# Revit family: Wenger Cabinet 04
name_source: partatom
category: Furniture
revit_build: Autodesk Revit Architecture 2012 (Build: 20110916_2132(x64)
units: mm (PartAtom-declared; Revit-internal decimal feet)

## types (4) — shared parameters
Cabinet Height = 7' - 1 5/8"
Manufacturer = Wenger Corporation
URL = http://www.wengercorp.com

## per-type parameters (varying)
| type | Cabinet Back Thickness | Cabinet Depth | Cabinet Label | Cabinet Width | Model |
| Standard Cabinet #4 | 0' - 0 3/4" | 2' - 5 1/4" | Labels : Standard | 2' - 3 1/2" | 04 |
| Narrow Cabinet #4 | 0' - 0 3/4" | 2' - 5 1/4" | Labels : Narrow | 1' - 9 1/2" | 04N |
| Acoustic Cabinet #4 | 0' - 3 1/4" | 2' - 7 3/4" | Labels : Acoustic | 2' - 3 1/2" | 04A |
| Narrow Acoustic Cabinet #4 | 0' - 3 1/4" | 2' - 7 3/4" | Labels : Narrow Acoustic | 1' - 9 1/2" | 04NA |

note: column(s) folded — value = type name in every type: Description

## geometry (parser evidence)
native form markers: Blend x6, Sweep x7
no freeform markers — native parametric forms only
